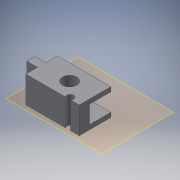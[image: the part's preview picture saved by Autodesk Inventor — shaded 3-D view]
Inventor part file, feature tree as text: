
AUTODESK INVENTOR PART (.ipt)
format: ipt  version: 2017 (Build 210142000, 142)  size: 132,608 bytes
history: native  units: mm
features: reference x5, other x4, extrude x3, sketch x3, plane x1, projected_geometry x1
ambient origin geometry x8: Origin, YZ Plane, XZ Plane, XY Plane, X Axis, Y Axis, Z Axis, Center Point
bodies: Solid1 (feature_tree)
feature tree (17):
  plane  "Work Plane1"
  extrude  "Extrusion1"  Depth=15.0mm TaperAngle=0.0deg
  extrude  "Extrusion2"  Depth=10.0mm TaperAngle=0.0deg
  extrude  "Extrusion3"  [1 undecoded]
  sketch  "Sketch1"  dims[d0=0.2mm d1=15.0mm d2=0.0mm]
  reference  "Reference1"
  reference  "Reference2"
  reference  "Reference3"
  sketch  "Sketch2"  dims[d3=15.0mm d4=0.0mm d5=10.0mm d6=0.0mm]
  reference  "Reference4"
  sketch  "Sketch3"
  projected_geometry  "Projected Loop1"
  reference  "Reference5"
  parser-record x1  (decoder bookkeeping rows leaked as tree rows — omitted from the tree; the rows remain in map.json)
  other  "gearbox.iam"
  other  "shifter box 1:1"
  other  "short selector:1"
note: 1 required parameter value undecoded (feature->parameter linkage not recoverable at this tier; creation-order binding heuristic only, values carry confidence <= 0.55)
note: 1 file-system path scrubbed to <path> (originals preserved in map.json)
